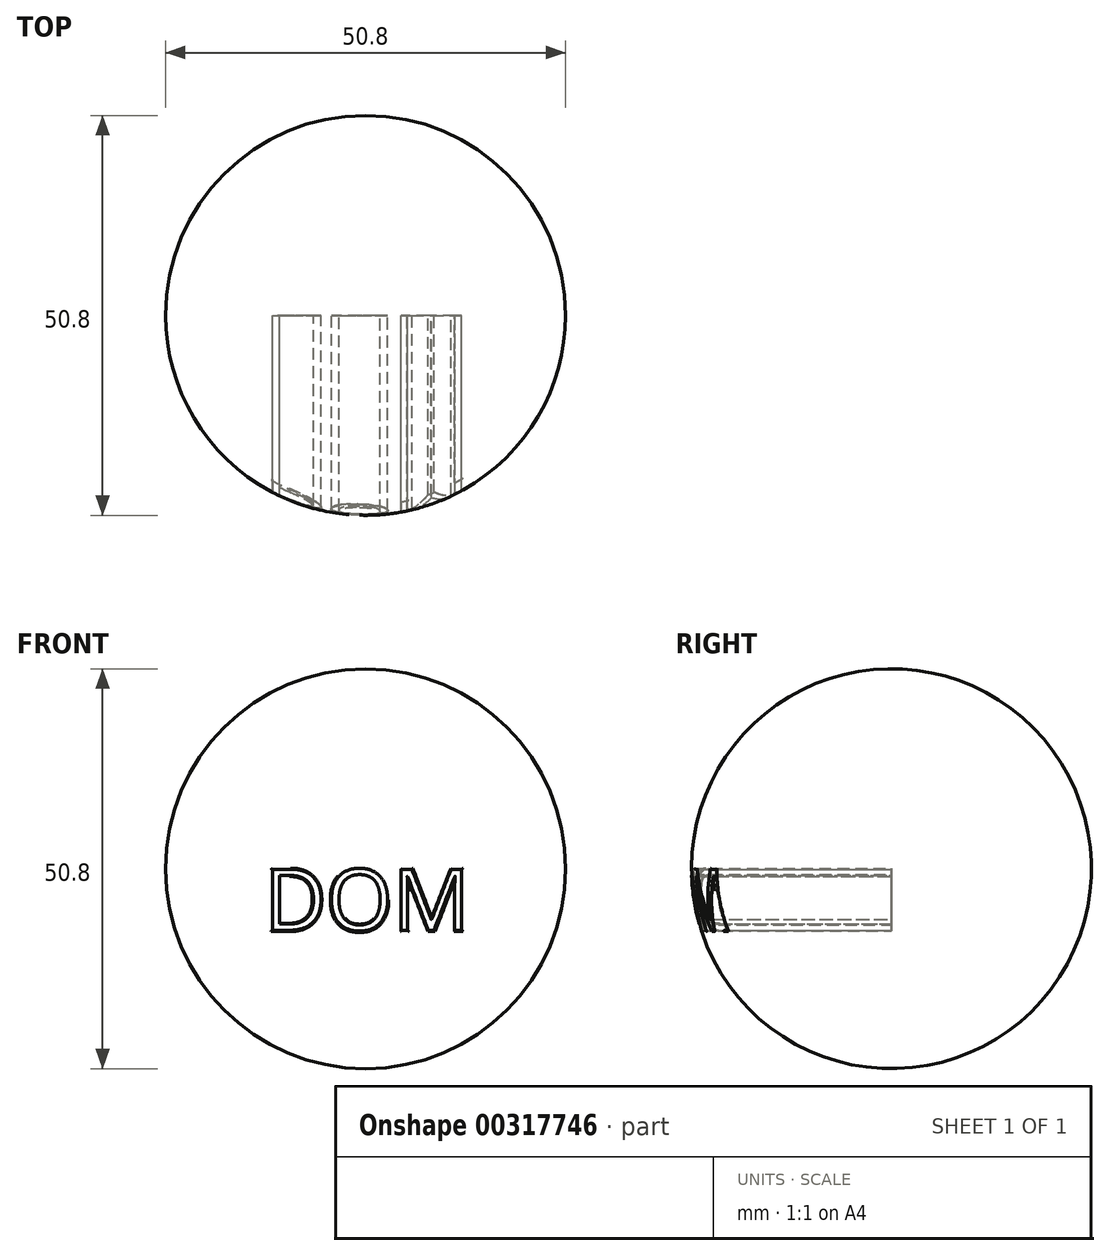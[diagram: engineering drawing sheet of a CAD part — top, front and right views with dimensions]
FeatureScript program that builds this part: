
annotation { "Feature Type Name" : "Feature", "Feature Type Description" : "" }
export const myFeature = defineFeature(function(context is Context, id is Id, definition is map)
    precondition{}
    {
        {
            var Q0;
            Q0=qCreatedBy(makeId("Front.planeOp"),FACE);
            var sketch = newSketch(context, id + "F0", { "sketchPlane" : qUnion([Q0])});
            skLineSegment(sketch, "E0", {"start": v(-25.4, 0) * mm, "end": v(25.4, 0) * mm});
            skArc(sketch, "E1", {"start": v(25.4, 0) * mm, "mid": v(0, 25.4) * mm, "end": v(-25.4, 0) * mm});
            skSolve(sketch);
        }
        {
            var Q0;
            Q0=makeQuery(id+"F0.imprint","IMPRINT",FACE,{"disambiguationData":[TD([[makeQuery(id+"F0.imprint","IMPRINT",EDGE,{"derivedFrom":sQuery(id+"F0.wireOp",EDGE,"E0")}),1.0]])]});
            var Q1;
            Q1=sQuery(id+"F0.wireOp",EDGE,"E0");
            revolve(context, id + "F1", {"entities" : qUnion([Q0]), "axis" : qUnion([Q1]), "revolveType" : RevolveType.FULL});
        }
        {
            var Q0;
            Q0=qCreatedBy(makeId("Front.planeOp"),FACE);
            var sketch = newSketch(context, id + "F2", { "sketchPlane" : qUnion([Q0])});
            skText(sketch, "E2", { "text": "DOM", "fontName": "OpenSans-Regular.ttf"});
            const initialGuessF2  = {"E2": [-0.01291, -0.00782, 1, 0, 0.00782]};
            skSetInitialGuess(sketch, initialGuessF2);
            skSolve(sketch);
        }
        {
            var Q0;
            Q0 = qSketchRegion(id + "F2", true);
            extrude(context, id + "F3", {"entities" : qUnion([Q0]), "operationType" : NewBodyOperationType.REMOVE, "depth" : 59.18 * mm});
        }
        {
            var Q0;
            Q0=makeQuery(id+"F3.boolean.opBoolean","INTERSECT",EDGE,{"derivedFrom":[makeQuery(id+"F1.opRevolve","SWEPT_FACE",FACE,{"disambiguationData":[OSD([sQuery(id+"F0.wireOp",EDGE,"E1")])]}),makeQuery(id+"F3.opExtrude","SWEPT_FACE",FACE,{"disambiguationData":[OSD([sQuery(id+"F2.wireOp",EDGE,"E2.sketch_text.stroke-8")])]})]});
            var Q1;
            Q1=makeQuery(id+"F3.boolean.opBoolean","INTERSECT",EDGE,{"derivedFrom":[makeQuery(id+"F1.opRevolve","SWEPT_FACE",FACE,{"disambiguationData":[OSD([sQuery(id+"F0.wireOp",EDGE,"E1")])]}),makeQuery(id+"F3.opExtrude","SWEPT_FACE",FACE,{"disambiguationData":[OSD([sQuery(id+"F2.wireOp",EDGE,"E2.sketch_text.stroke-9")])]})]});
            var Q2;
            Q2=makeQuery(id+"F3.boolean.opBoolean","INTERSECT",EDGE,{"derivedFrom":[makeQuery(id+"F1.opRevolve","SWEPT_FACE",FACE,{"disambiguationData":[OSD([sQuery(id+"F0.wireOp",EDGE,"E1")])]}),makeQuery(id+"F3.opExtrude","SWEPT_FACE",FACE,{"disambiguationData":[OSD([sQuery(id+"F2.wireOp",EDGE,"E2.sketch_text.stroke-10")])]})]});
            var Q3;
            Q3=makeQuery(id+"F3.boolean.opBoolean","INTERSECT",EDGE,{"derivedFrom":[makeQuery(id+"F1.opRevolve","SWEPT_FACE",FACE,{"disambiguationData":[OSD([sQuery(id+"F0.wireOp",EDGE,"E1")])]}),makeQuery(id+"F3.opExtrude","SWEPT_FACE",FACE,{"disambiguationData":[OSD([sQuery(id+"F2.wireOp",EDGE,"E2.sketch_text.stroke-6")])]})]});
            var Q4;
            Q4=makeQuery(id+"F3.boolean.opBoolean","INTERSECT",EDGE,{"derivedFrom":[makeQuery(id+"F1.opRevolve","SWEPT_FACE",FACE,{"disambiguationData":[OSD([sQuery(id+"F0.wireOp",EDGE,"E1")])]}),makeQuery(id+"F3.opExtrude","SWEPT_FACE",FACE,{"disambiguationData":[OSD([sQuery(id+"F2.wireOp",EDGE,"E2.sketch_text.stroke-5")])]})]});
            var Q5;
            Q5=makeQuery(id+"F3.boolean.opBoolean","INTERSECT",EDGE,{"derivedFrom":[makeQuery(id+"F1.opRevolve","SWEPT_FACE",FACE,{"disambiguationData":[OSD([sQuery(id+"F0.wireOp",EDGE,"E1")])]}),makeQuery(id+"F3.opExtrude","SWEPT_FACE",FACE,{"disambiguationData":[OSD([sQuery(id+"F2.wireOp",EDGE,"E2.sketch_text.stroke-3")])]})]});
            var Q6;
            Q6=makeQuery(id+"F3.boolean.opBoolean","INTERSECT",EDGE,{"derivedFrom":[makeQuery(id+"F1.opRevolve","SWEPT_FACE",FACE,{"disambiguationData":[OSD([sQuery(id+"F0.wireOp",EDGE,"E1")])]}),makeQuery(id+"F3.opExtrude","SWEPT_FACE",FACE,{"disambiguationData":[OSD([sQuery(id+"F2.wireOp",EDGE,"E2.sketch_text.stroke-0")])]})]});
            var Q7;
            Q7=makeQuery(id+"F3.boolean.opBoolean","INTERSECT",EDGE,{"derivedFrom":[makeQuery(id+"F1.opRevolve","SWEPT_FACE",FACE,{"disambiguationData":[OSD([sQuery(id+"F0.wireOp",EDGE,"E1")])]}),makeQuery(id+"F3.opExtrude","SWEPT_FACE",FACE,{"disambiguationData":[OSD([sQuery(id+"F2.wireOp",EDGE,"E2.sketch_text.stroke-17")])]})]});
            var Q8;
            Q8=makeQuery(id+"F3.boolean.opBoolean","INTERSECT",EDGE,{"derivedFrom":[makeQuery(id+"F1.opRevolve","SWEPT_FACE",FACE,{"disambiguationData":[OSD([sQuery(id+"F0.wireOp",EDGE,"E1")])]}),makeQuery(id+"F3.opExtrude","SWEPT_FACE",FACE,{"disambiguationData":[OSD([sQuery(id+"F2.wireOp",EDGE,"E2.sketch_text.stroke-18")])]})]});
            var Q9;
            Q9=makeQuery(id+"F3.boolean.opBoolean","INTERSECT",EDGE,{"derivedFrom":[makeQuery(id+"F1.opRevolve","SWEPT_FACE",FACE,{"disambiguationData":[OSD([sQuery(id+"F0.wireOp",EDGE,"E1")])]}),makeQuery(id+"F3.opExtrude","SWEPT_FACE",FACE,{"disambiguationData":[OSD([sQuery(id+"F2.wireOp",EDGE,"E2.sketch_text.stroke-19")])]})]});
            var Q10;
            Q10=makeQuery(id+"F3.boolean.opBoolean","INTERSECT",EDGE,{"derivedFrom":[makeQuery(id+"F1.opRevolve","SWEPT_FACE",FACE,{"disambiguationData":[OSD([sQuery(id+"F0.wireOp",EDGE,"E1")])]}),makeQuery(id+"F3.opExtrude","SWEPT_FACE",FACE,{"disambiguationData":[OSD([sQuery(id+"F2.wireOp",EDGE,"E2.sketch_text.stroke-20")])]})]});
            var Q11;
            Q11=makeQuery(id+"F3.boolean.opBoolean","INTERSECT",EDGE,{"derivedFrom":[makeQuery(id+"F1.opRevolve","SWEPT_FACE",FACE,{"disambiguationData":[OSD([sQuery(id+"F0.wireOp",EDGE,"E1")])]}),makeQuery(id+"F3.opExtrude","SWEPT_FACE",FACE,{"disambiguationData":[OSD([sQuery(id+"F2.wireOp",EDGE,"E2.sketch_text.stroke-21")])]})]});
            var Q12;
            Q12=makeQuery(id+"F3.boolean.opBoolean","INTERSECT",EDGE,{"derivedFrom":[makeQuery(id+"F1.opRevolve","SWEPT_FACE",FACE,{"disambiguationData":[OSD([sQuery(id+"F0.wireOp",EDGE,"E1")])]}),makeQuery(id+"F3.opExtrude","SWEPT_FACE",FACE,{"disambiguationData":[OSD([sQuery(id+"F2.wireOp",EDGE,"E2.sketch_text.stroke-14")])]})]});
            var Q13;
            Q13=makeQuery(id+"F3.boolean.opBoolean","INTERSECT",EDGE,{"derivedFrom":[makeQuery(id+"F1.opRevolve","SWEPT_FACE",FACE,{"disambiguationData":[OSD([sQuery(id+"F0.wireOp",EDGE,"E1")])]}),makeQuery(id+"F3.opExtrude","SWEPT_FACE",FACE,{"disambiguationData":[OSD([sQuery(id+"F2.wireOp",EDGE,"E2.sketch_text.stroke-15")])]})]});
            var Q14;
            Q14=makeQuery(id+"F3.boolean.opBoolean","INTERSECT",EDGE,{"derivedFrom":[makeQuery(id+"F1.opRevolve","SWEPT_FACE",FACE,{"disambiguationData":[OSD([sQuery(id+"F0.wireOp",EDGE,"E1")])]}),makeQuery(id+"F3.opExtrude","SWEPT_FACE",FACE,{"disambiguationData":[OSD([sQuery(id+"F2.wireOp",EDGE,"E2.sketch_text.stroke-16")])]})]});
            var Q15;
            Q15=makeQuery(id+"F3.boolean.opBoolean","INTERSECT",EDGE,{"derivedFrom":[makeQuery(id+"F1.opRevolve","SWEPT_FACE",FACE,{"disambiguationData":[OSD([sQuery(id+"F0.wireOp",EDGE,"E1")])]}),makeQuery(id+"F3.opExtrude","SWEPT_FACE",FACE,{"disambiguationData":[OSD([sQuery(id+"F2.wireOp",EDGE,"E2.sketch_text.stroke-22")])]})]});
            var Q16;
            Q16=makeQuery(id+"F3.boolean.opBoolean","INTERSECT",EDGE,{"derivedFrom":[makeQuery(id+"F1.opRevolve","SWEPT_FACE",FACE,{"disambiguationData":[OSD([sQuery(id+"F0.wireOp",EDGE,"E1")])]}),makeQuery(id+"F3.opExtrude","SWEPT_FACE",FACE,{"disambiguationData":[OSD([sQuery(id+"F2.wireOp",EDGE,"E2.sketch_text.stroke-35")])]})]});
            var Q17;
            Q17=makeQuery(id+"F3.boolean.opBoolean","INTERSECT",EDGE,{"derivedFrom":[makeQuery(id+"F1.opRevolve","SWEPT_FACE",FACE,{"disambiguationData":[OSD([sQuery(id+"F0.wireOp",EDGE,"E1")])]}),makeQuery(id+"F3.opExtrude","SWEPT_FACE",FACE,{"disambiguationData":[OSD([sQuery(id+"F2.wireOp",EDGE,"E2.sketch_text.stroke-33")])]})]});
            var Q18;
            Q18=makeQuery(id+"F3.boolean.opBoolean","INTERSECT",EDGE,{"derivedFrom":[makeQuery(id+"F1.opRevolve","SWEPT_FACE",FACE,{"disambiguationData":[OSD([sQuery(id+"F0.wireOp",EDGE,"E1")])]}),makeQuery(id+"F3.opExtrude","SWEPT_FACE",FACE,{"disambiguationData":[OSD([sQuery(id+"F2.wireOp",EDGE,"E2.sketch_text.stroke-30")])]})]});
            var Q19;
            Q19=makeQuery(id+"F3.boolean.opBoolean","INTERSECT",EDGE,{"derivedFrom":[makeQuery(id+"F1.opRevolve","SWEPT_FACE",FACE,{"disambiguationData":[OSD([sQuery(id+"F0.wireOp",EDGE,"E1")])]}),makeQuery(id+"F3.opExtrude","SWEPT_FACE",FACE,{"disambiguationData":[OSD([sQuery(id+"F2.wireOp",EDGE,"E2.sketch_text.stroke-37")])]})]});
            var Q20;
            Q20=makeQuery(id+"F3.boolean.opBoolean","INTERSECT",EDGE,{"derivedFrom":[makeQuery(id+"F1.opRevolve","SWEPT_FACE",FACE,{"disambiguationData":[OSD([sQuery(id+"F0.wireOp",EDGE,"E1")])]}),makeQuery(id+"F3.opExtrude","SWEPT_FACE",FACE,{"disambiguationData":[OSD([sQuery(id+"F2.wireOp",EDGE,"E2.sketch_text.stroke-36")])]})]});
            var Q21;
            Q21=makeQuery(id+"F3.boolean.opBoolean","INTERSECT",EDGE,{"derivedFrom":[makeQuery(id+"F1.opRevolve","SWEPT_FACE",FACE,{"disambiguationData":[OSD([sQuery(id+"F0.wireOp",EDGE,"E1")])]}),makeQuery(id+"F3.opExtrude","SWEPT_FACE",FACE,{"disambiguationData":[OSD([sQuery(id+"F2.wireOp",EDGE,"E2.sketch_text.stroke-39")])]})]});
            var Q22;
            Q22=makeQuery(id+"F3.boolean.opBoolean","INTERSECT",EDGE,{"derivedFrom":[makeQuery(id+"F1.opRevolve","SWEPT_FACE",FACE,{"disambiguationData":[OSD([sQuery(id+"F0.wireOp",EDGE,"E1")])]}),makeQuery(id+"F3.opExtrude","SWEPT_FACE",FACE,{"disambiguationData":[OSD([sQuery(id+"F2.wireOp",EDGE,"E2.sketch_text.stroke-46")])]})]});
            var Q23;
            Q23=makeQuery(id+"F3.boolean.opBoolean","INTERSECT",EDGE,{"derivedFrom":[makeQuery(id+"F1.opRevolve","SWEPT_FACE",FACE,{"disambiguationData":[OSD([sQuery(id+"F0.wireOp",EDGE,"E1")])]}),makeQuery(id+"F3.opExtrude","SWEPT_FACE",FACE,{"disambiguationData":[OSD([sQuery(id+"F2.wireOp",EDGE,"E2.sketch_text.stroke-47")])]})]});
            var Q24;
            Q24=makeQuery(id+"F3.boolean.opBoolean","INTERSECT",EDGE,{"derivedFrom":[makeQuery(id+"F1.opRevolve","SWEPT_FACE",FACE,{"disambiguationData":[OSD([sQuery(id+"F0.wireOp",EDGE,"E1")])]}),makeQuery(id+"F3.opExtrude","SWEPT_FACE",FACE,{"disambiguationData":[OSD([sQuery(id+"F2.wireOp",EDGE,"E2.sketch_text.stroke-34")])]})]});
            var Q25;
            Q25=makeQuery(id+"F3.boolean.opBoolean","INTERSECT",EDGE,{"derivedFrom":[makeQuery(id+"F1.opRevolve","SWEPT_FACE",FACE,{"disambiguationData":[OSD([sQuery(id+"F0.wireOp",EDGE,"E1")])]}),makeQuery(id+"F3.opExtrude","SWEPT_FACE",FACE,{"disambiguationData":[OSD([sQuery(id+"F2.wireOp",EDGE,"E2.sketch_text.stroke-42")])]})]});
            var Q26;
            Q26=makeQuery(id+"F3.boolean.opBoolean","INTERSECT",EDGE,{"derivedFrom":[makeQuery(id+"F1.opRevolve","SWEPT_FACE",FACE,{"disambiguationData":[OSD([sQuery(id+"F0.wireOp",EDGE,"E1")])]}),makeQuery(id+"F3.opExtrude","SWEPT_FACE",FACE,{"disambiguationData":[OSD([sQuery(id+"F2.wireOp",EDGE,"E2.sketch_text.stroke-41")])]})]});
            var Q27;
            Q27=makeQuery(id+"F3.boolean.opBoolean","INTERSECT",EDGE,{"derivedFrom":[makeQuery(id+"F1.opRevolve","SWEPT_FACE",FACE,{"disambiguationData":[OSD([sQuery(id+"F0.wireOp",EDGE,"E1")])]}),makeQuery(id+"F3.opExtrude","SWEPT_FACE",FACE,{"disambiguationData":[OSD([sQuery(id+"F2.wireOp",EDGE,"E2.sketch_text.stroke-43")])]})]});
            var Q28;
            Q28=makeQuery(id+"F3.boolean.opBoolean","INTERSECT",EDGE,{"derivedFrom":[makeQuery(id+"F1.opRevolve","SWEPT_FACE",FACE,{"disambiguationData":[OSD([sQuery(id+"F0.wireOp",EDGE,"E1")])]}),makeQuery(id+"F3.opExtrude","SWEPT_FACE",FACE,{"disambiguationData":[OSD([sQuery(id+"F2.wireOp",EDGE,"E2.sketch_text.stroke-40")])]})]});
            fillet(context, id + "F4", {"entities" : qUnion([Q0, Q1, Q2, Q3, Q4, Q5, Q6, Q7, Q8, Q9, Q10, Q11, Q12, Q13, Q14, Q15, Q16, Q17, Q18, Q19, Q20, Q21, Q22, Q23, Q24, Q25, Q26, Q27, Q28]), "radius" : 0.13 * mm, "tangentPropagation" : true, "allowEdgeOverflow" : false});
        }
    });
